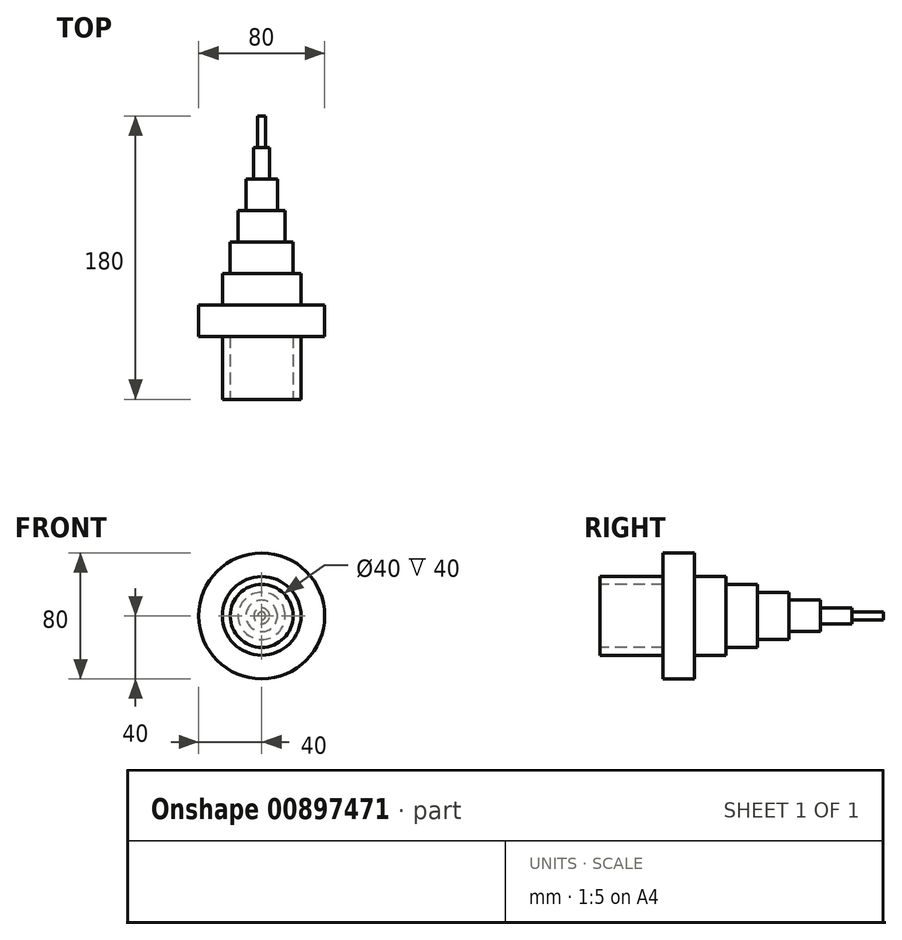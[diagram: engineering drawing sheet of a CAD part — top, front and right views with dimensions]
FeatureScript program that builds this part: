
annotation { "Feature Type Name" : "Feature", "Feature Type Description" : "" }
export const myFeature = defineFeature(function(context is Context, id is Id, definition is map)
    precondition{}
    {
        {
            var Q0;
            Q0=qCreatedBy(makeId("Front.planeOp"),FACE);
            var sketch = newSketch(context, id + "F0", { "sketchPlane" : qUnion([Q0])});
            skCircle(sketch, "E0", {"center": v(0, 0) * mm, "radius": 40 * mm});
            skSolve(sketch);
        }
        {
            var Q0;
            Q0 = qSketchRegion(id + "F0", true);
            extrude(context, id + "F1", {"entities" : qUnion([Q0]), "depth" : 20 * mm, "offsetDistance" : 25.4 * mm});
        }
        {
            var Q0;
            Q0=makeQuery(id+"F1.opExtrude","CAP_FACE",FACE,{"disambiguationData":[OSD([sQuery(id+"F0.wireOp",EDGE,"E0")])],"isStart":false});
            var sketch = newSketch(context, id + "F2", { "sketchPlane" : qUnion([Q0])});
            skCircle(sketch, "E1", {"center": v(0, 0) * mm, "radius": 25 * mm});
            skSolve(sketch);
        }
        {
            var Q0;
            Q0=makeQuery(id+"F0.imprint","IMPRINT",FACE,{"disambiguationData":[TD([[makeQuery(id+"F0.imprint","IMPRINT",EDGE,{"derivedFrom":sQuery(id+"F0.wireOp",EDGE,"E0")}),1.0]])]});
            var sketch = newSketch(context, id + "F3", { "sketchPlane" : qUnion([Q0])});
            skCircle(sketch, "E2", {"center": v(0, 0) * mm, "radius": 25 * mm});
            skSolve(sketch);
        }
        {
            var Q0;
            Q0=sQuery(id+"F3.wireOp",EDGE,"E2");
            extrude(context, id + "F4", {"bodyType" : ToolBodyType.SURFACE, "surfaceEntities" : qUnion([Q0]), "depth" : 40 * mm, "offsetDistance" : 25.4 * mm});
        }
        {
            var Q0;
            Q0=makeQuery(id+"F2.imprint","IMPRINT",FACE,{"disambiguationData":[TD([[makeQuery(id+"F2.imprint","IMPRINT",EDGE,{"derivedFrom":sQuery(id+"F2.wireOp",EDGE,"E1")}),1.0]])]});
            extrude(context, id + "F5", {"entities" : qUnion([Q0]), "operationType" : NewBodyOperationType.ADD, "depth" : 40 * mm, "offsetDistance" : 25.4 * mm});
        }
        {
            var Q0;
            Q0 = qSketchRegion(id + "F3", true);
            var Q1;
            Q1=sQuery(id+"F3.wireOp",EDGE,"E2");
            extrude(context, id + "F6", {"entities" : qUnion([Q0]), "operationType" : NewBodyOperationType.ADD, "surfaceOperationType" : NewSurfaceOperationType.ADD, "surfaceEntities" : qUnion([Q1]), "depth" : 25.4 * mm, "offsetDistance" : 25.4 * mm});
        }
        {
            var Q0;
            Q0=makeQuery(id+"F3.imprint","IMPRINT",FACE,{"disambiguationData":[TD([[makeQuery(id+"F3.imprint","IMPRINT",EDGE,{"derivedFrom":sQuery(id+"F3.wireOp",EDGE,"E2")}),1.0]])]});
            var Q1;
            Q1=sQuery(id+"F3.wireOp",EDGE,"E2");
            extrude(context, id + "F7", {"entities" : qUnion([Q0]), "operationType" : NewBodyOperationType.ADD, "surfaceOperationType" : NewSurfaceOperationType.ADD, "surfaceEntities" : qUnion([Q1]), "oppositeDirection" : true, "depth" : 20 * mm, "offsetDistance" : 25.4 * mm});
        }
        {
            var Q0;
            Q0=makeQuery(id+"F7.opExtrude","CAP_FACE",FACE,{"disambiguationData":[OSD([sQuery(id+"F3.wireOp",EDGE,"E2")])],"isStart":false});
            var sketch = newSketch(context, id + "F8", { "sketchPlane" : qUnion([Q0])});
            skCircle(sketch, "E3", {"center": v(0, 0) * mm, "radius": 20 * mm});
            skSolve(sketch);
        }
        {
            var Q0;
            Q0=makeQuery(id+"F8.imprint","IMPRINT",FACE,{"disambiguationData":[TD([[makeQuery(id+"F8.imprint","IMPRINT",EDGE,{"derivedFrom":sQuery(id+"F8.wireOp",EDGE,"E3")}),1.0]])]});
            extrude(context, id + "F9", {"entities" : qUnion([Q0]), "operationType" : NewBodyOperationType.ADD, "depth" : 20 * mm, "offsetDistance" : 25.4 * mm});
        }
        {
            var Q0;
            Q0=makeQuery(id+"F9.opExtrude","CAP_FACE",FACE,{"disambiguationData":[OSD([sQuery(id+"F8.wireOp",EDGE,"E3")])],"isStart":false});
            var sketch = newSketch(context, id + "F10", { "sketchPlane" : qUnion([Q0])});
            skCircle(sketch, "E4", {"center": v(0, 0) * mm, "radius": 15 * mm});
            skSolve(sketch);
        }
        {
            var Q0;
            Q0=makeQuery(id+"F10.imprint","IMPRINT",FACE,{"disambiguationData":[TD([[makeQuery(id+"F10.imprint","IMPRINT",EDGE,{"derivedFrom":sQuery(id+"F10.wireOp",EDGE,"E4")}),1.0]])]});
            extrude(context, id + "F11", {"entities" : qUnion([Q0]), "operationType" : NewBodyOperationType.ADD, "depth" : 20 * mm, "offsetDistance" : 25.4 * mm});
        }
        {
            var Q0;
            Q0=makeQuery(id+"F11.opExtrude","CAP_FACE",FACE,{"disambiguationData":[OSD([sQuery(id+"F10.wireOp",EDGE,"E4")])],"isStart":false});
            var sketch = newSketch(context, id + "F12", { "sketchPlane" : qUnion([Q0])});
            skCircle(sketch, "E5", {"center": v(0, 0) * mm, "radius": 10 * mm});
            skSolve(sketch);
        }
        {
            var Q0;
            Q0=makeQuery(id+"F12.imprint","IMPRINT",FACE,{"disambiguationData":[TD([[makeQuery(id+"F12.imprint","IMPRINT",EDGE,{"derivedFrom":sQuery(id+"F12.wireOp",EDGE,"E5")}),1.0]])]});
            extrude(context, id + "F13", {"entities" : qUnion([Q0]), "operationType" : NewBodyOperationType.ADD, "depth" : 20 * mm, "offsetDistance" : 25.4 * mm});
        }
        {
            var Q0;
            Q0=makeQuery(id+"F13.opExtrude","CAP_FACE",FACE,{"disambiguationData":[OSD([sQuery(id+"F12.wireOp",EDGE,"E5")])],"isStart":false});
            var sketch = newSketch(context, id + "F14", { "sketchPlane" : qUnion([Q0])});
            skCircle(sketch, "E6", {"center": v(0, 0) * mm, "radius": 5 * mm});
            skSolve(sketch);
        }
        {
            var Q0;
            Q0=makeQuery(id+"F14.imprint","IMPRINT",FACE,{"disambiguationData":[TD([[makeQuery(id+"F14.imprint","IMPRINT",EDGE,{"derivedFrom":sQuery(id+"F14.wireOp",EDGE,"E6")}),1.0]])]});
            extrude(context, id + "F15", {"entities" : qUnion([Q0]), "operationType" : NewBodyOperationType.ADD, "depth" : 20 * mm, "offsetDistance" : 25.4 * mm});
        }
        {
            var Q0;
            Q0=makeQuery(id+"F15.opExtrude","CAP_FACE",FACE,{"disambiguationData":[OSD([sQuery(id+"F14.wireOp",EDGE,"E6")])],"isStart":false});
            var sketch = newSketch(context, id + "F16", { "sketchPlane" : qUnion([Q0])});
            skCircle(sketch, "E7", {"center": v(0, 0) * mm, "radius": 2.5 * mm});
            skSolve(sketch);
        }
        {
            var Q0;
            Q0=makeQuery(id+"F16.imprint","IMPRINT",FACE,{"disambiguationData":[TD([[makeQuery(id+"F16.imprint","IMPRINT",EDGE,{"derivedFrom":sQuery(id+"F16.wireOp",EDGE,"E7")}),1.0]])]});
            extrude(context, id + "F17", {"entities" : qUnion([Q0]), "operationType" : NewBodyOperationType.ADD, "depth" : 20 * mm, "offsetDistance" : 25.4 * mm});
        }
        {
            var Q0;
            Q0=makeQuery(id+"F5.opExtrude","CAP_FACE",FACE,{"disambiguationData":[OSD([sQuery(id+"F2.wireOp",EDGE,"E1")])],"isStart":false});
            var sketch = newSketch(context, id + "F18", { "sketchPlane" : qUnion([Q0])});
            skCircle(sketch, "E8", {"center": v(0, 0) * mm, "radius": 20 * mm});
            skSolve(sketch);
        }
        {
            var Q0;
            Q0=makeQuery(id+"F18.imprint","IMPRINT",FACE,{"disambiguationData":[TD([[makeQuery(id+"F18.imprint","IMPRINT",EDGE,{"derivedFrom":sQuery(id+"F18.wireOp",EDGE,"E8")}),1.0]])]});
            extrude(context, id + "F19", {"entities" : qUnion([Q0]), "operationType" : NewBodyOperationType.REMOVE, "oppositeDirection" : true, "depth" : 40 * mm, "offsetDistance" : 25.4 * mm});
        }
    });
